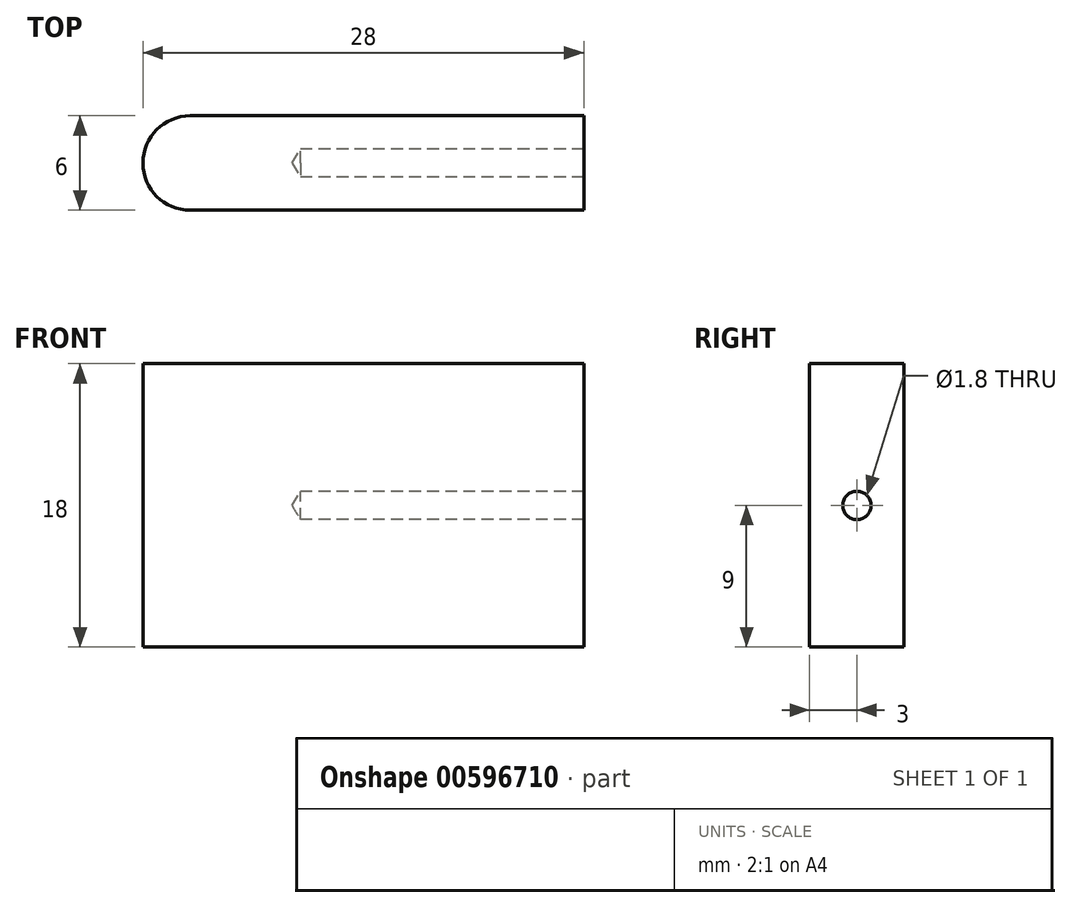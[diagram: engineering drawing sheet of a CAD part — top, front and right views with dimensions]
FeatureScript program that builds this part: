
annotation { "Feature Type Name" : "Feature", "Feature Type Description" : "" }
export const myFeature = defineFeature(function(context is Context, id is Id, definition is map)
    precondition{}
    {
        {
            var Q0;
            Q0=qCreatedBy(makeId("Top.planeOp"),FACE);
            var sketch = newSketch(context, id + "F0", { "sketchPlane" : qUnion([Q0])});
            skLineSegment(sketch, "E0.bottom", {"start": v(-11, 3) * mm, "end": v(14, 3) * mm});
            skLineSegment(sketch, "E0.top", {"start": v(-11, -3) * mm, "end": v(14, -3) * mm});
            skLineSegment(sketch, "E0.right", {"start": v(14, 3) * mm, "end": v(14, -3) * mm});
            skPoint(sketch, "E0.middle", {"position": v(0, 0) * mm});
            skPoint(sketch, "E1", {"position": v(-11, 0) * mm});
            skArc(sketch, "E2", {"start": v(-11, 3) * mm, "mid": v(-14, 0) * mm, "end": v(-11, -3) * mm});
            skSolve(sketch);
        }
        {
            var Q0;
            Q0=makeQuery(id+"F0.imprint","IMPRINT",FACE,{"disambiguationData":[TD([[makeQuery(id+"F0.imprint","IMPRINT",EDGE,{"derivedFrom":sQuery(id+"F0.wireOp",EDGE,"E0.bottom")}),-1.0]])]});
            extrude(context, id + "F1", {"entities" : qUnion([Q0]), "depth" : 18 * mm, "offsetDistance" : 25 * mm});
        }
        {
            var Q0;
            Q0=makeQuery(id+"F1.opExtrude","SWEPT_FACE",FACE,{"disambiguationData":[OSD([sQuery(id+"F0.wireOp",EDGE,"E0.right")])]});
            var sketch = newSketch(context, id + "F2", { "sketchPlane" : qUnion([Q0])});
            skPoint(sketch, "E3", {"position": v(0, 9) * mm});
            skCircle(sketch, "E4", {"center": v(0, 9) * mm, "radius": 0.9 * mm});
            skSolve(sketch);
        }
        {
            var Q0;
            Q0=sQuery(id+"F2.wireOp",VERTEX,"E3");
            var Q1;
            Q1=makeQuery(id+"F1.opExtrude","SWEPT_BODY",BODY,{"disambiguationData":[OSD([sQuery(id+"F0.wireOp",EDGE,"E0.bottom"),sQuery(id+"F0.wireOp",EDGE,"E0.top"),sQuery(id+"F0.wireOp",EDGE,"E0.right"),sQuery(id+"F0.wireOp",EDGE,"9d4P5nyE-twoF-418v-SjNd-5uESCs2DruYY")])]});
            hole(context, id + "F3", {"style" : HoleStyle.SIMPLE, "endStyle" : HoleEndStyle.BLIND, "holeDiameter" : 1.8 * mm, "majorDiameter" : 5 * mm, "holeDepth" : 18 * mm, "isTappedThrough" : true, "tappedDepth" : 12 * mm, "tapClearance" : 3, "startFromSketch" : true, "locations" : qUnion([Q0]), "scope" : qUnion([Q1])});
        }
        {
            var Q0;
            Q0=qCreatedBy(makeId("Right.planeOp"),FACE);
            cPlane(context, id + "F4", {"entities" : qUnion([Q0]), "cplaneType" : CPlaneType.OFFSET, "offset" : 14 * mm, "oppositeDirection" : true, "width" : 150 * mm, "height" : 150 * mm});
        }
    });
